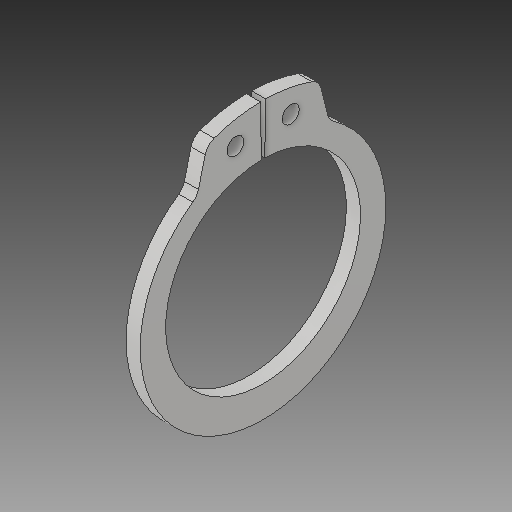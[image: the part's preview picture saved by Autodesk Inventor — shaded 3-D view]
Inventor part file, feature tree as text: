
AUTODESK INVENTOR PART (.ipt)
format: ipt  version: 2019 (Build 230136000, 136)  size: 111,616 bytes
history: native  units: in
note: dims shown in document units (in); Inventor stores cm internally (conversion verified against a paired STEP export)
features: fillet x1
ambient origin geometry x8: Origin, YZ Plane, XZ Plane, XY Plane, X Axis, Y Axis, Z Axis, Center Point
bodies: Solid1 (feature_tree)
feature tree (1):
  fillet  "Fillet1"  [1 undecoded]
note: 1 required parameter value undecoded (feature->parameter linkage not recoverable at this tier; creation-order binding heuristic only, values carry confidence <= 0.55)
